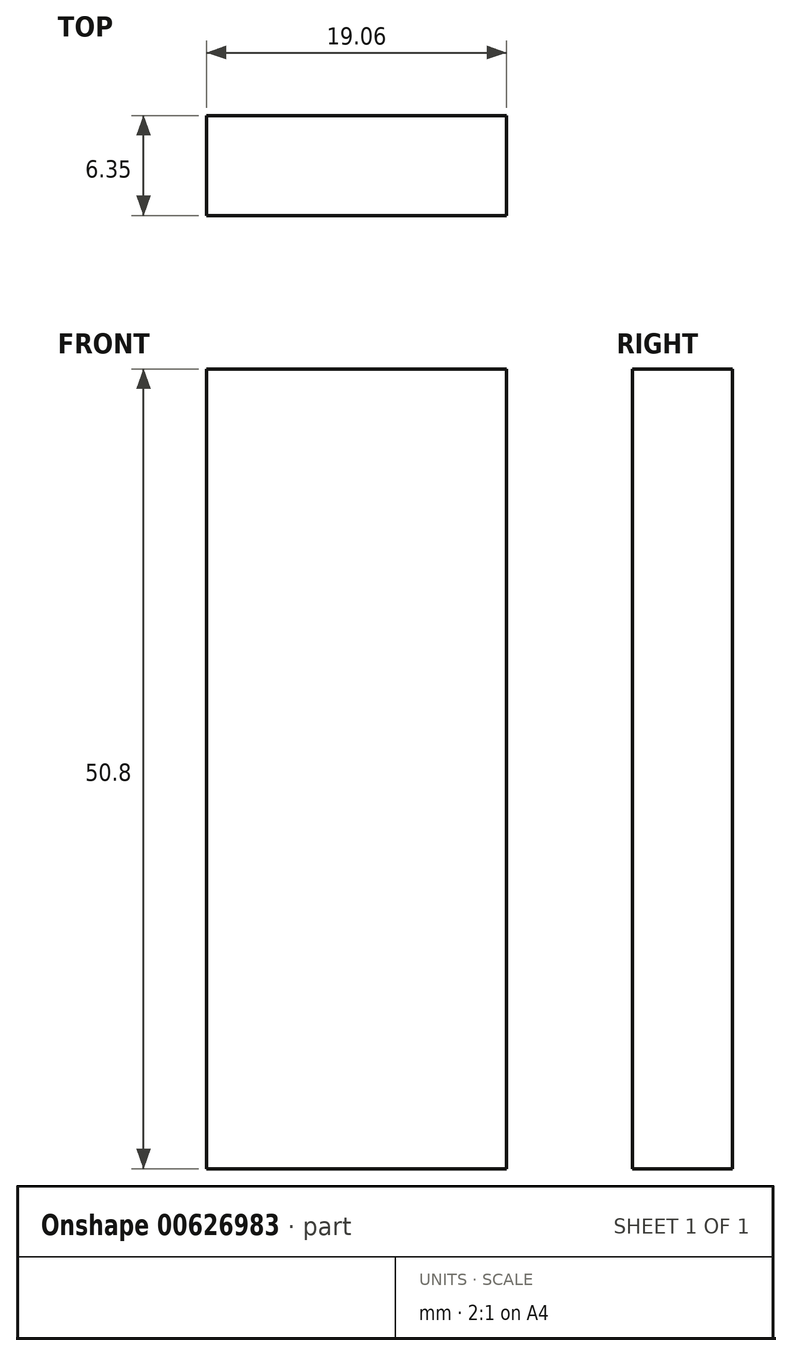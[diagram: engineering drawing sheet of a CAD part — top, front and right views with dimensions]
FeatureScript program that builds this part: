
annotation { "Feature Type Name" : "Feature", "Feature Type Description" : "" }
export const myFeature = defineFeature(function(context is Context, id is Id, definition is map)
    precondition{}
    {
        {
            var Q0;
            Q0=qCreatedBy(makeId("Front.planeOp"),FACE);
            var sketch = newSketch(context, id + "F0", { "sketchPlane" : qUnion([Q0])});
            skLineSegment(sketch, "E0.bottom", {"start": v(9.53, -25.4) * mm, "end": v(-9.52, -25.4) * mm});
            skLineSegment(sketch, "E0.top", {"start": v(9.53, 25.4) * mm, "end": v(-9.52, 25.4) * mm});
            skLineSegment(sketch, "E0.left", {"start": v(9.53, -25.4) * mm, "end": v(9.53, 25.4) * mm});
            skLineSegment(sketch, "E0.right", {"start": v(-9.52, -25.4) * mm, "end": v(-9.52, 25.4) * mm});
            skPoint(sketch, "E0.middle", {"position": v(0, 0) * mm});
            skSolve(sketch);
        }
        {
            var Q0;
            Q0 = qSketchRegion(id + "F0", true);
            extrude(context, id + "F1", {"entities" : qUnion([Q0]), "depth" : 6.35 * mm, "offsetDistance" : 25.4 * mm});
        }
    });
